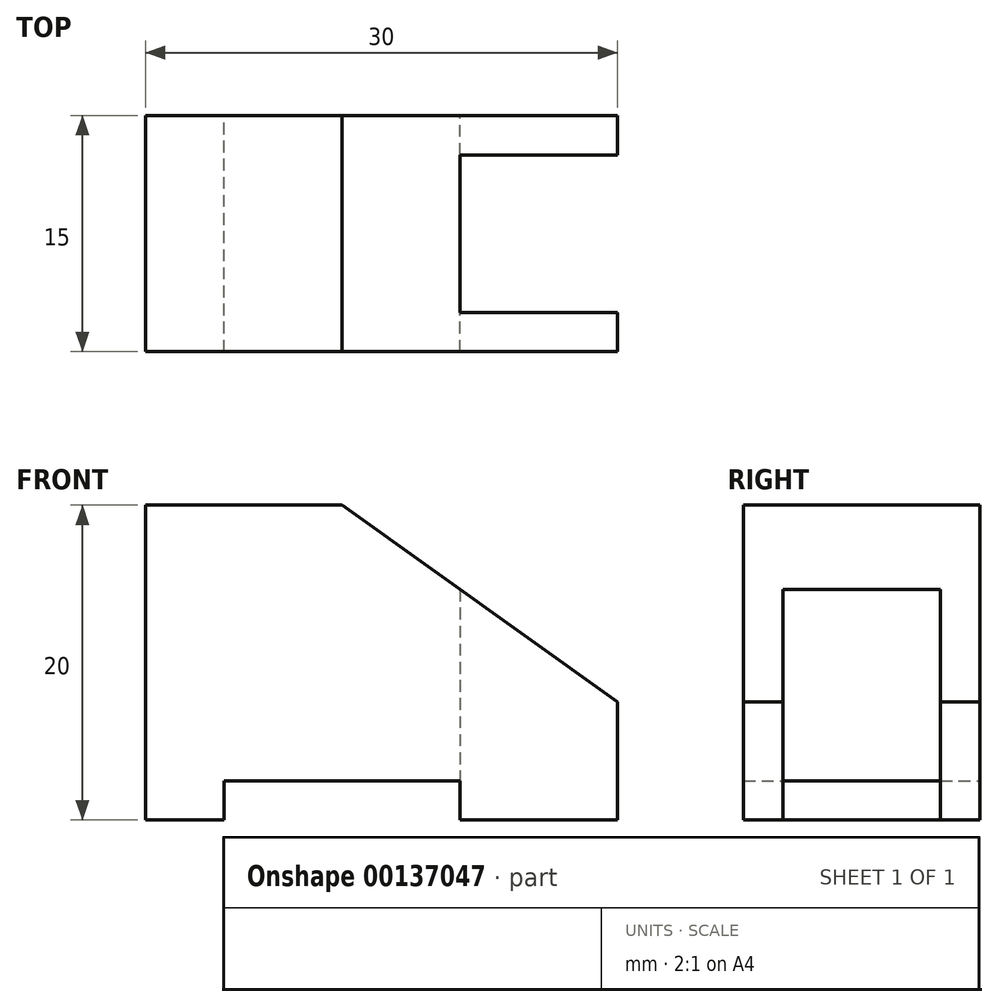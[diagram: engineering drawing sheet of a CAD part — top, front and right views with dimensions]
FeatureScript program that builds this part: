
annotation { "Feature Type Name" : "Feature", "Feature Type Description" : "" }
export const myFeature = defineFeature(function(context is Context, id is Id, definition is map)
    precondition{}
    {
        {
            var Q0;
            Q0=qCreatedBy(makeId("Front.planeOp"),FACE);
            var sketch = newSketch(context, id + "F0", { "sketchPlane" : qUnion([Q0])});
            skLineSegment(sketch, "E0", {"start": v(0, 0) * mm, "end": v(0, 20) * mm});
            skLineSegment(sketch, "E1", {"start": v(0, 20) * mm, "end": v(12.5, 20) * mm});
            skLineSegment(sketch, "E2", {"start": v(12.5, 20) * mm, "end": v(30, 7.5) * mm});
            skLineSegment(sketch, "E3", {"start": v(30, 7.5) * mm, "end": v(30, 0) * mm});
            skLineSegment(sketch, "E4", {"start": v(30, 0) * mm, "end": v(20, 0) * mm});
            skLineSegment(sketch, "E5", {"start": v(20, 0) * mm, "end": v(20, 2.5) * mm});
            skLineSegment(sketch, "E6", {"start": v(20, 2.5) * mm, "end": v(5, 2.5) * mm});
            skLineSegment(sketch, "E7", {"start": v(5, 2.5) * mm, "end": v(5, 0) * mm});
            skLineSegment(sketch, "E8", {"start": v(5, 0) * mm, "end": v(0, 0) * mm});
            skSolve(sketch);
        }
        {
            var Q0;
            Q0=makeQuery(id+"F0.imprint","IMPRINT",FACE,{"disambiguationData":[TD([[makeQuery(id+"F0.imprint","IMPRINT",EDGE,{"derivedFrom":sQuery(id+"F0.wireOp",EDGE,"E0")}),-1.0]])]});
            extrude(context, id + "F1", {"entities" : qUnion([Q0]), "depth" : 15 * mm});
        }
        {
            var Q0;
            Q0=qCreatedBy(makeId("Top.planeOp"),FACE);
            var sketch = newSketch(context, id + "F2", { "sketchPlane" : qUnion([Q0])});
            skLineSegment(sketch, "E9.bottom", {"start": v(0, 0) * mm, "end": v(12.5, 0) * mm});
            skLineSegment(sketch, "E9.top", {"start": v(0, -15) * mm, "end": v(12.5, -15) * mm});
            skLineSegment(sketch, "E9.left", {"start": v(0, 0) * mm, "end": v(0, -15) * mm});
            skLineSegment(sketch, "E9.right", {"start": v(12.5, 0) * mm, "end": v(12.5, -15) * mm});
            skLineSegment(sketch, "E10.bottom", {"start": v(12.5, 0) * mm, "end": v(30, 0) * mm});
            skLineSegment(sketch, "E10.top", {"start": v(12.5, -15) * mm, "end": v(30, -15) * mm});
            skLineSegment(sketch, "E10.right", {"start": v(30, 0) * mm, "end": v(30, -15) * mm});
            skLineSegment(sketch, "E11", {"start": v(30, -12.5) * mm, "end": v(20, -12.5) * mm});
            skLineSegment(sketch, "E12", {"start": v(20, -12.5) * mm, "end": v(20, -2.5) * mm});
            skLineSegment(sketch, "E13", {"start": v(20, -2.5) * mm, "end": v(30, -2.5) * mm});
            skLineSegment(sketch, "E14", {"start": v(30, -12.5) * mm, "end": v(30, -2.5) * mm});
            skSolve(sketch);
        }
        {
            var Q0;
            Q0=makeQuery(id+"F2.imprint","IMPRINT",FACE,{"disambiguationData":[TD([[makeQuery(id+"F2.imprint","IMPRINT",EDGE,{"derivedFrom":sQuery(id+"F2.wireOp",EDGE,"E11")}),-1.0]])]});
            extrude(context, id + "F3", {"entities" : qUnion([Q0]), "operationType" : NewBodyOperationType.REMOVE, "depth" : 25 * mm});
        }
    });
